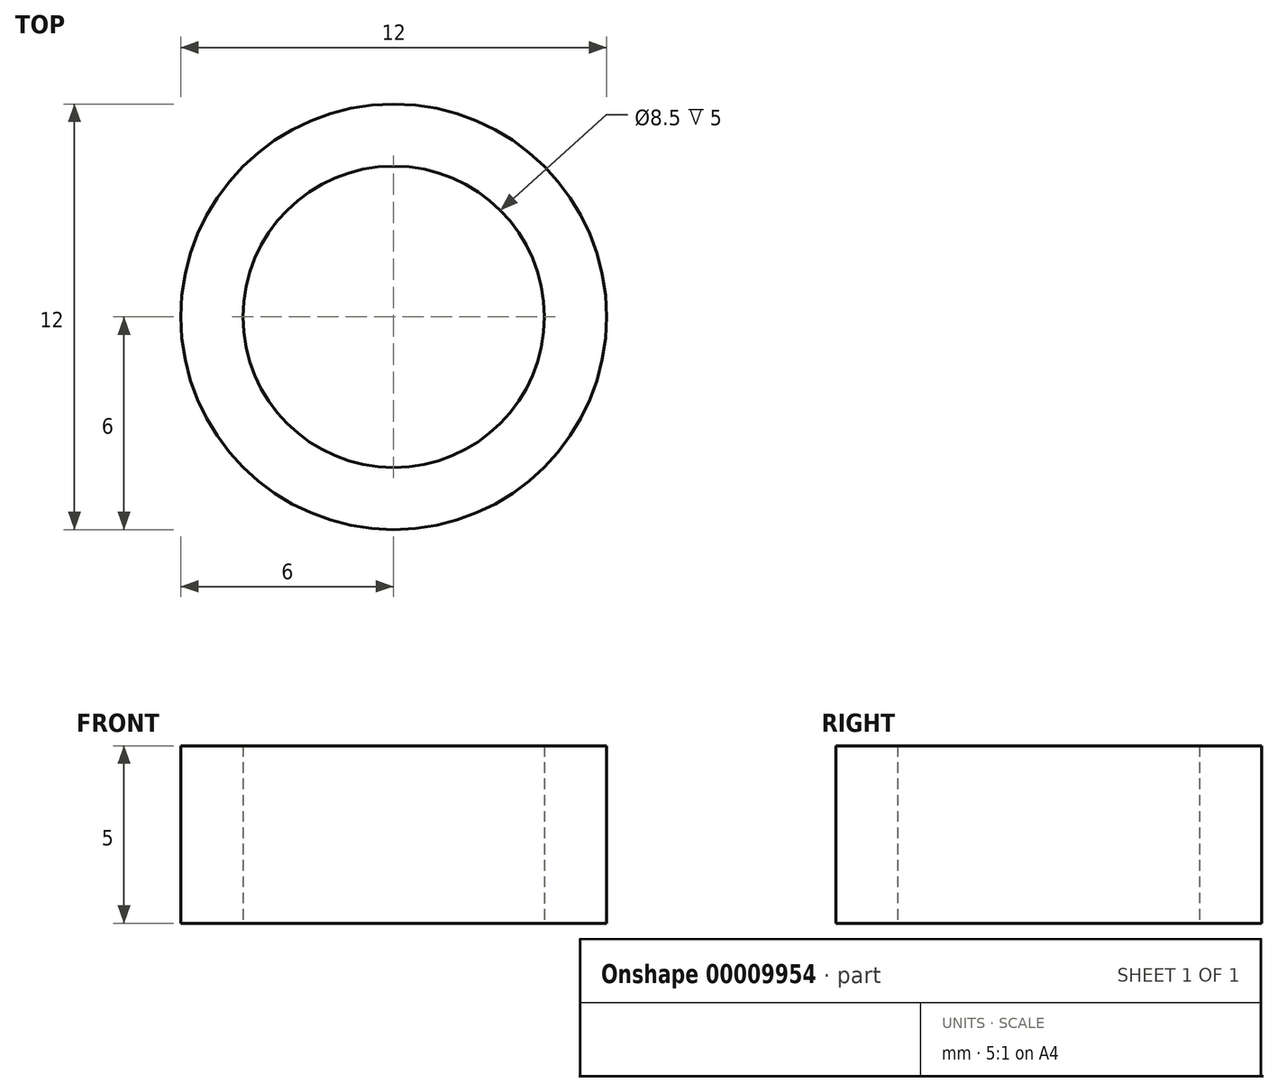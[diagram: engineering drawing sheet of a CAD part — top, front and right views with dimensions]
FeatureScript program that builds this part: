
annotation { "Feature Type Name" : "Feature", "Feature Type Description" : "" }
export const myFeature = defineFeature(function(context is Context, id is Id, definition is map)
    precondition{}
    {
        {
            var Q0;
            Q0=qCreatedBy(makeId("Top.planeOp"),FACE);
            var sketch = newSketch(context, id + "F0", { "sketchPlane" : qUnion([Q0])});
            skCircle(sketch, "E0", {"center": v(0, 0) * mm, "radius": 6 * mm});
            skCircle(sketch, "E1", {"center": v(0, 0) * mm, "radius": 4.25 * mm});
            skSolve(sketch);
        }
        {
            var Q0;
            Q0=qSketchRegion(id+"F0",true);
            extrude(context, id + "F1", {"entities" : qUnion([Q0]), "depth" : 5 * mm});
        }
    });
